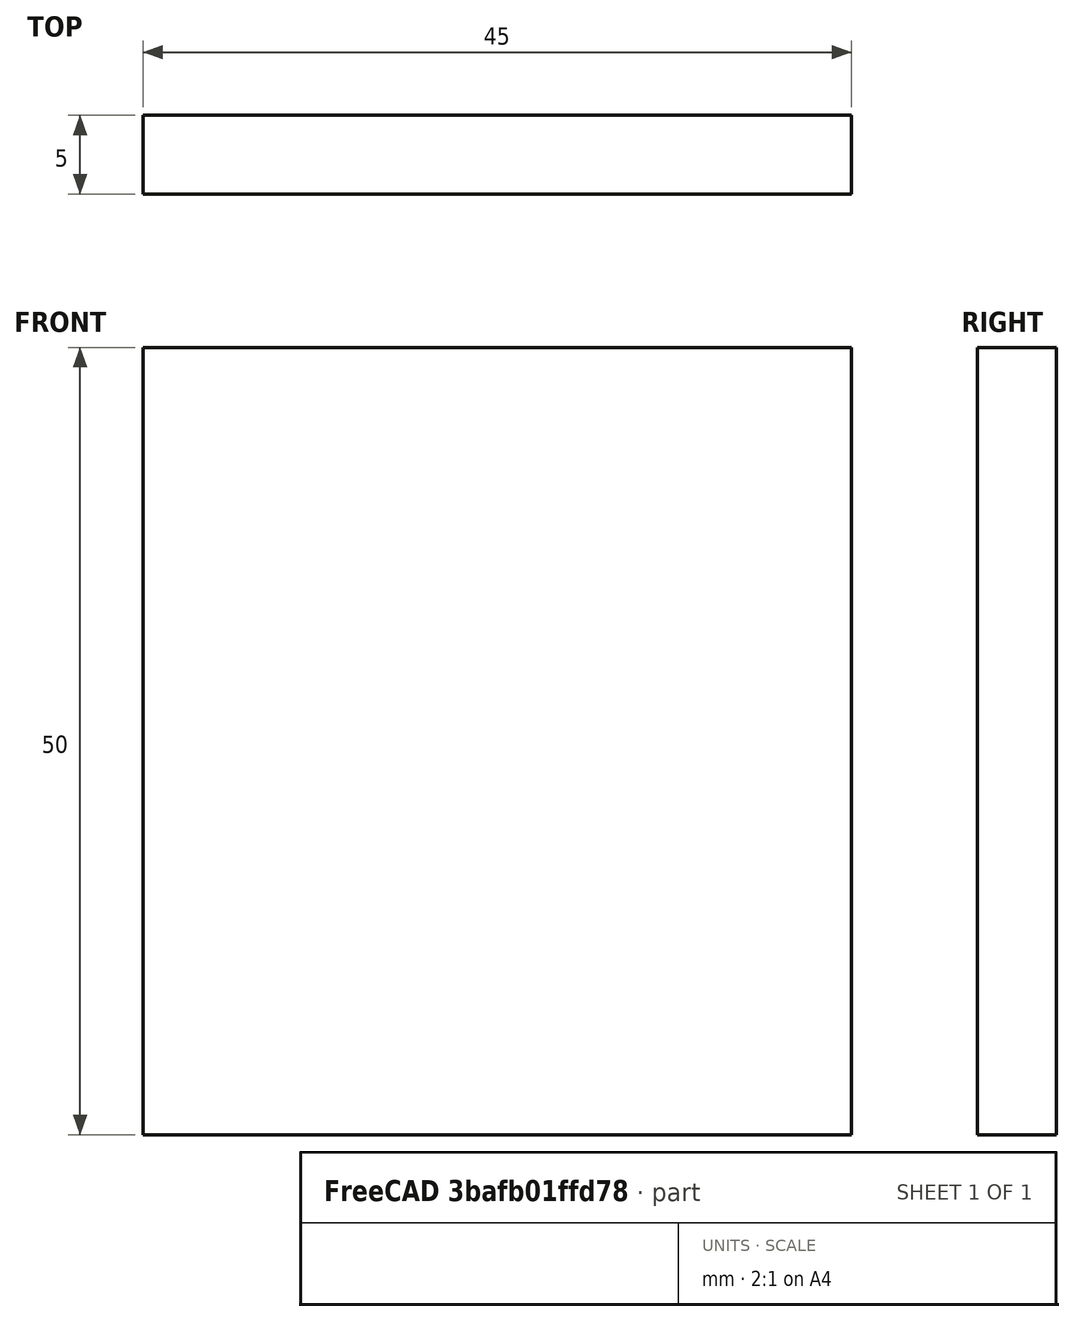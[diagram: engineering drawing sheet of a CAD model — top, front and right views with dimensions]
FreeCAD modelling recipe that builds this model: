
FCSTD DOCUMENT  (FreeCAD 0.15R4671 (Git))
Label: Flat Bar 45x5 EN10058 S235JR
License: All rights reserved
LicenseURL: http://en.wikipedia.org/wiki/All_rights_reserved
objects: Sketcher::SketchObject×1, Part::Extrusion×1
note: 2 computed .brp shape members not serialized (recipe doc carries the construction recipe); baked Part::Feature solids carry a one-line shape summary decoded from their .brp

FEATURE [Sketcher::SketchObject] Sketch
  sketch-geometry (4):
    g0: LineSegment StartX=-22.5 StartY=-2.5 StartZ=0 EndX=22.5 EndY=-2.5 EndZ=0
    g1: LineSegment StartX=22.5 StartY=-2.5 StartZ=0 EndX=22.5 EndY=2.5 EndZ=0
    g2: LineSegment StartX=22.5 StartY=2.5 StartZ=0 EndX=-22.5 EndY=2.5 EndZ=0
    g3: LineSegment StartX=-22.5 StartY=2.5 StartZ=0 EndX=-22.5 EndY=-2.5 EndZ=0
  constraints (12):
    c: Coincident(g0,g1)
    c: Coincident(g1,g2)
    c: Coincident(g2,g3)
    c: Coincident(g3,g0)
    c: Horizontal(g0)
    c: Horizontal(g2)
    c: Vertical(g1)
    c: Vertical(g3)
    c: Symmetric(g1,g2,g-2)
    c: Symmetric(g0,g1,g-1)
    c: DistanceY(g1) = 5
    c: DistanceX(g0) = 45
FEATURE [Part::Extrusion] Extrude  label="Flat Bar 45x5 EN10058 S235JR"
  Base = -> Sketch
  Dir = (0,0,50)
  Solid = true
